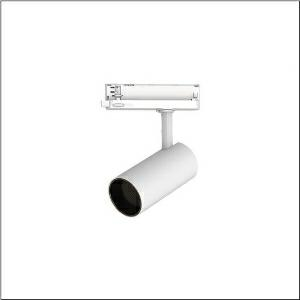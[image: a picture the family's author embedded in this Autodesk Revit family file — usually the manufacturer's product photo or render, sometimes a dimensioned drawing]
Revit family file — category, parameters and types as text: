
# Revit family: spot_31_slim_51sf117fb3b
name_source: partatom
category: Lighting Fixtures
units: mm (PartAtom-declared; Revit-internal decimal feet)

## family parameters
Cut with Voids When Loaded = No
Host = Face
Light Source = No
Part Type = Normal
Room Calculation Point = No
Round Connector Dimension = Use Diameter
Shared = No

## types (1)
- Spot 31 Slim (1 x LED, 2180 lm, 23.7 W, 3000K)
    Apparent Load = 24 VA
    CIE Flux Codes = 99 100 100 100 100
    Color Rendering = 90
    Color Temperature = 3000K
    Default Elevation = 1800 mm
    Description = Spot 31 Slim, directional spotlight, light control with reflector, of aluminium, anti glare with honeycomb louvre, LED rated luminous flux: 2.200lm, light colour: 930, control gear: ECG, with 3-phase adapter, mains connection: 220..240V, AC, 50/60Hz, housing, of aluminium, traffic white (RAL 9016), diameter: 70mm, adapter, of plastic, protection rating (complete): IP20, insulation class (complete): insulation class I (protective earthing), certification: CE, impact resistance: IK02, packaging unit: 1 piece
    Height = 210 mm
    Lamp = 1 x LED
    Lamp Light Flux = 2180 lm
    Lamp Power = 23.7 W
    Lamp count = 1
    Length = 70 mm
    Luminous efficacy = 92 lm/W
    Manufacturer = Siteco
    ModVariant = No
    Model = 51SF117FB3B
    Mounting Place = Ceiling
    Mounting Type = Pendant
    Number of Poles = 1
    OnlyDefault = Yes
    Power Factor = 1
    Product Name = Spot 31 Slim
    Product group = directional spotlight
    ProductGroupID = 906
    Protection Class = Protection class I
    Protection Degree = IP 20
    RLX_Detail_Level = 1
    RLX_Emergency_Light_Flux = 0 lm
    RLX_Emergency_Type = 0
    RLX_Emergency_Type_DB = No
    RlxData = <blob elided: 14277 chars, md5=79518f02>
    Socket = socket
    Standby Power = 0 W
    System Light Flux = 2180 lm
    System Power = 24 W
    Type Comments = Product without accessories
    Type Image = l_1228472.jpg
    URL = http://relux.com
    VarID = ---
    Voltage = 0 V
    Weight = 0.00 kg
    Width = 0 mm  [stored 0 ft]

note: [stored X ft] marks values corroborated as IEEE doubles in the binary element streams (Revit-internal decimal feet)

## geometry (parser evidence)
native form markers: Sweep x9
no freeform markers — native parametric forms only
